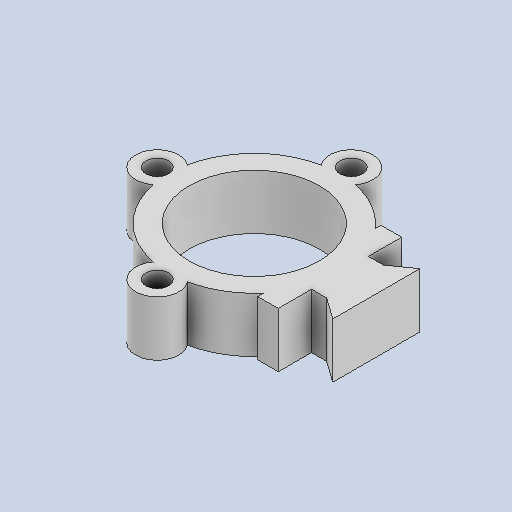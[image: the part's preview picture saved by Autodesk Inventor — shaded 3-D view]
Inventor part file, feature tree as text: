
AUTODESK INVENTOR PART (.ipt)
format: ipt  version: 2024 (Build 280153000, 153)  size: 333,824 bytes
history: native  units: mm
features: other x1, extrude x1, sketch x1
ambient origin geometry x8: Origin, YZ Plane, XZ Plane, XY Plane, X Axis, Y Axis, Z Axis, Center Point
bodies: Body1 (feature_tree)
feature tree (3):
  other  "Sólido1"
  extrude  "Extrusión1"  Depth=8.3mm
  sketch  "Boceto1"  dims[d0=12.7mm d1=8.3mm d2=3.1mm d3=2.2mm d4=18.0mm d5=3.0mm d6=19.0mm d7=25.0mm d8=3.3mm d9=6.3mm d10=20.0mm d12=90.0deg d14=20.0mm d16=90.0deg d18=8.0mm d19=0.0mm]
